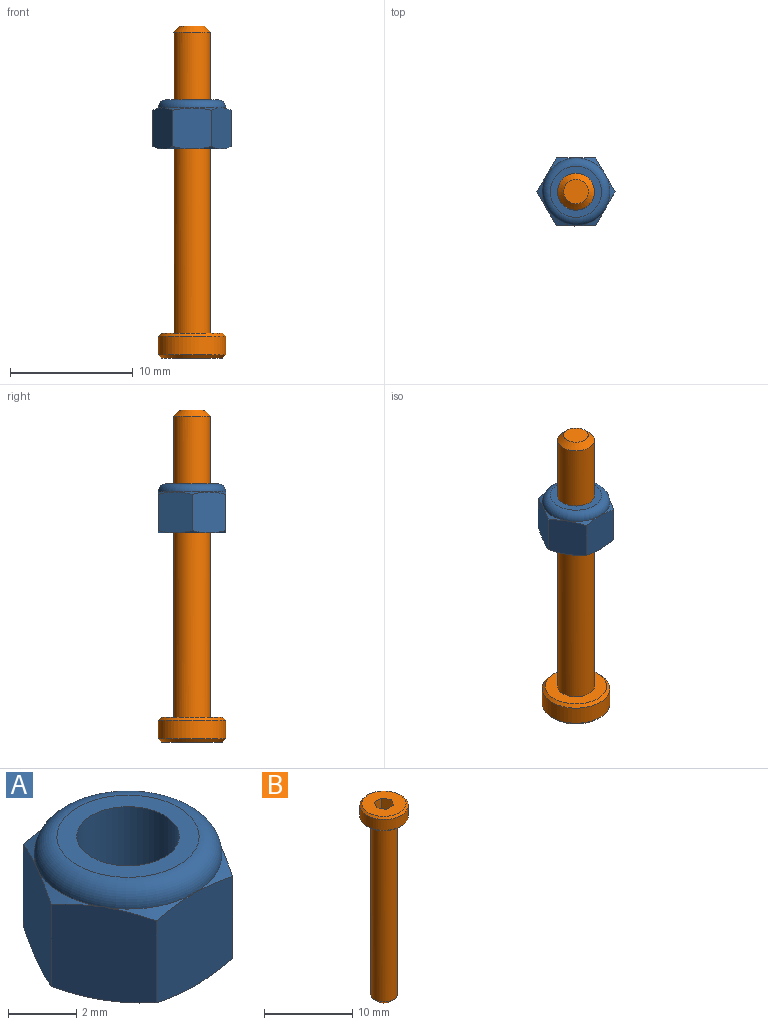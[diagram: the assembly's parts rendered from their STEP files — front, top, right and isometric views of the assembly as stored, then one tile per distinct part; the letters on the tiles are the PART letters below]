
ASSEMBLY  parts=2 mates=1
PART A: 22 faces, bbox 6.6x6.6x4.2 mm
  f0: plane 3.59x2.99mm, normal (-0.87,0.5,0), area 10.2mm2, adj f1,f5,f7,f9,f13,f14,f16,f21
  f1: plane 3.59x2.99mm, normal (-0.87,-0.5,0), area 10.2mm2, adj f0,f2,f7,f9,f10,f14,f20,f21
  f2: plane 3.6x3.42mm, normal (0,-1,0), area 10.2mm2, adj f1,f3,f7,f10,f11,f14,f19,f20
  f3: plane 3.59x2.99mm, normal (0.87,-0.5,0), area 10.2mm2, adj f2,f4,f7,f11,f12,f14,f18,f19
  f4: plane 3.59x2.99mm, normal (0.87,0.5,0), area 10.2mm2, adj f3,f5,f7,f12,f14,f15,f17,f18
  f5: plane 3.6x3.42mm, normal (0,1,0), area 10.2mm2, adj f0,f4,f7,f13,f14,f15,f16,f17
  f6: plane 4.17x4.17mm, normal (0,0,1), area 6.6mm2, adj f8,f14
  f7: plane 5.5x5.5mm, normal (0,0,-1), area 16.7mm2, adj f0,f1,f2,f3,f4,f5,f8,f16
  f8: cylinder r=1.5mm len=4mm, axis (0,0,1), area 37.7mm2, adj f6,f7
  f9: cone r=3.18mm half-angle=65deg, axis (0,0,-1), area 0.7mm2, adj f0,f1,f14
  f10: cone r=3.18mm half-angle=65deg, axis (0,0,-1), area 0.7mm2, adj f1,f2,f14
  f11: cone r=3.18mm half-angle=65deg, axis (0,0,-1), area 0.7mm2, adj f2,f3,f14
  f12: cone r=3.18mm half-angle=65deg, axis (0,0,-1), area 0.7mm2, adj f3,f4,f14
  f13: cone r=3.18mm half-angle=65deg, axis (0,0,-1), area 0.7mm2, adj f0,f5,f14
  f14: torus R=2.08mm, axis (0,0,-1), area 16.5mm2, adj f0,f1,f2,f3,f4,f5,f6,f9
  f15: cone r=3.18mm half-angle=65deg, axis (0,0,-1), area 0.7mm2, adj f4,f5,f14
  f16: cone r=2.75mm half-angle=65deg, axis (0,0,1), area 0.7mm2, adj f0,f5,f7
  f17: cone r=2.75mm half-angle=65deg, axis (0,0,1), area 0.7mm2, adj f4,f5,f7
  f18: cone r=2.75mm half-angle=65deg, axis (0,0,1), area 0.7mm2, adj f3,f4,f7
  f19: cone r=2.75mm half-angle=65deg, axis (0,0,1), area 0.7mm2, adj f2,f3,f7
  f20: cone r=2.75mm half-angle=65deg, axis (0,0,1), area 0.7mm2, adj f1,f2,f7
  f21: cone r=2.75mm half-angle=65deg, axis (0,0,1), area 0.7mm2, adj f0,f1,f7
PART B: 15 faces, bbox 5.5x5.5x27 mm
  f0: plane 5x5mm, normal (0,0,1), area 16.2mm2, adj f3,f4,f5,f6,f7,f8,f11
  f1: cylinder r=2.75mm len=5.5mm, axis (0,0,-1), area 25.9mm2, adj f10,f11
  f2: plane 5x5mm, normal (0,0,-1), area 12.6mm2, adj f10,f12
  f3: plane 1.5x1mm, normal (-0.87,-0.5,0), area 1.7mm2, adj f0,f4,f8,f9
  f4: plane 1.5x1.15mm, normal (0,-1,0), area 1.7mm2, adj f0,f3,f5,f9
  f5: plane 1.5x1mm, normal (0.87,-0.5,0), area 1.7mm2, adj f0,f4,f6,f9
  f6: plane 1.5x1mm, normal (0.87,0.5,0), area 1.7mm2, adj f0,f5,f7,f9
  f7: plane 1.5x1.15mm, normal (0,1,0), area 1.7mm2, adj f0,f6,f8,f9
  f8: plane 1.5x1mm, normal (-0.87,0.5,0), area 1.7mm2, adj f0,f3,f7,f9
  f9: plane 2.31x2mm, normal (0,0,1), area 3.5mm2, adj f3,f4,f5,f6,f7,f8
  f10: cone r=2.75mm half-angle=45deg, axis (0,0,1), area 5.8mm2, adj f1,f2
  f11: cone r=2.5mm half-angle=45deg, axis (0,0,-1), area 5.8mm2, adj f0,f1
  f12: cylinder r=1.5mm len=24.5mm, axis (0,0,1), area 230.9mm2, adj f2,f14
  f13: plane 2x2mm, normal (0,0,-1), area 3.1mm2, adj f14
  f14: cone r=1mm half-angle=45deg, axis (0,0,1), area 5.6mm2, adj f12,f13
PLACE A t=(-22.55,-24.82,1.81)mm
PLACE B rot(axis=(1,0,0),180deg) t=(27.45,-24.82,-13.19)mm
MATE fastened B.f1 <-> A.f8  axis (0,0,1) through (-22.55,-24.82,-13.19)mm
